# Revit family: 0043110 Sylvania Lighting Fixture START ECO SURFACE IP44 520LM 840
name_source: partatom
category: Lighting Fixtures
revit_build: Autodesk Revit 2016 (Build: 20150220_1215(x64)
units: mm (PartAtom-declared; Revit-internal decimal feet)

## family parameters
Cut with Voids When Loaded = No
Host = Face
Light Source = Yes
OmniClass Number = 23.80.70.11.17
OmniClass Title = Specialized Lighting by Location or Use
Part Type = Normal
Room Calculation Point = No
Round Connector Dimension = Use Diameter
Shared = No

## types (1)
- 0043110 START ECO SURFACE IP44 520LM 840
    Apparent Load = 6 VA
    Assembly Code = D5020200
    AssetType = Fixed
    Color Filter = 16777215
    Default Elevation = 0 mm  [stored 0 ft]
    Description = Ceiling / wall luminaire with integrated LED  Perfect solution for hallways, circulation spaces or foyer.   Even and uniform light distribution with a halo lighting effect on the wall surface    6W 515 lumens Supplied with LED driver (non-dimmable)    IK03 PMMA diffuser   Low maintenance with 30,000 hours LED life expectancy
    Diameter_FEILO = 180 mm
    Dimming Lamp Color Temperature Shift = <None>
    DimmingControlOptions = Non dimmable
    DocumentationLiterature = http://www.sylvania-lighting.com
    DurationUnit = hours
    ElectricShockClassification = Class I
    ExpectedLife = 50000
    Height_FEILO = 75 mm
    IfcExportAs = IfcLightFixtureType
    IfcExportType = IfcLightFixtureType
    ImpactProtectionIndex = IK03
    IngressProtection = IP44
    InputNominalFrequency = 50 Hz
    InputVoltage = 220-240V~
    Keynote = 16500
    Lamp = LED
    LampColourRenderingIndex = 80
    LampColourTemperature = 4000 K
    LampMacAdamStep = 6
    LampNominalLuminous = 515 lm
    LampsType = LED
    LuminousEfficacy = 86 lm/W
    Manufacturer = Feilo Sylvania
    ManufacturerName = Feilo Sylvania
    Material = aluminium housing, polycarbonate diffuser
    Material_1_FEILO = <By Category>
    Material_2_FEILO = Metal_Sylvania_Sylcircle_White
    Material_3_FEILO = Polycarbonate_Sylvania_Sylcircle_Opal
    Material_4_FEILO = <By Category>
    Model = START ECO SURFACE IP44 520LM 840
    ModelNumber = 0043110
    ModelReference = START ECO SURFACE IP44 520LM 840
    Name = START ECO SURFACE IP44 520LM 840
    NominalHeight = 75 mm
    NominalLength = 180 mm
    NominalWidth = 0 mm  [stored 0 ft]
    Photometric Web File = 0043110.ies
    PowerConsumption = 6 W
    PowerFactor = 0.8
    Radius_FEILO = 90 mm  [stored 0.295276 ft]
    Tilt Angle = -90°
    TypeName = START ECO SURFACE IP44 520LM 840
    URL = http://www.sylvania-lighting.com
    Voltage = 230 V

note: [stored X ft] marks values corroborated as IEEE doubles in the binary element streams (Revit-internal decimal feet)

## geometry (parser evidence)
native form markers: Sweep x3
no freeform markers — native parametric forms only
